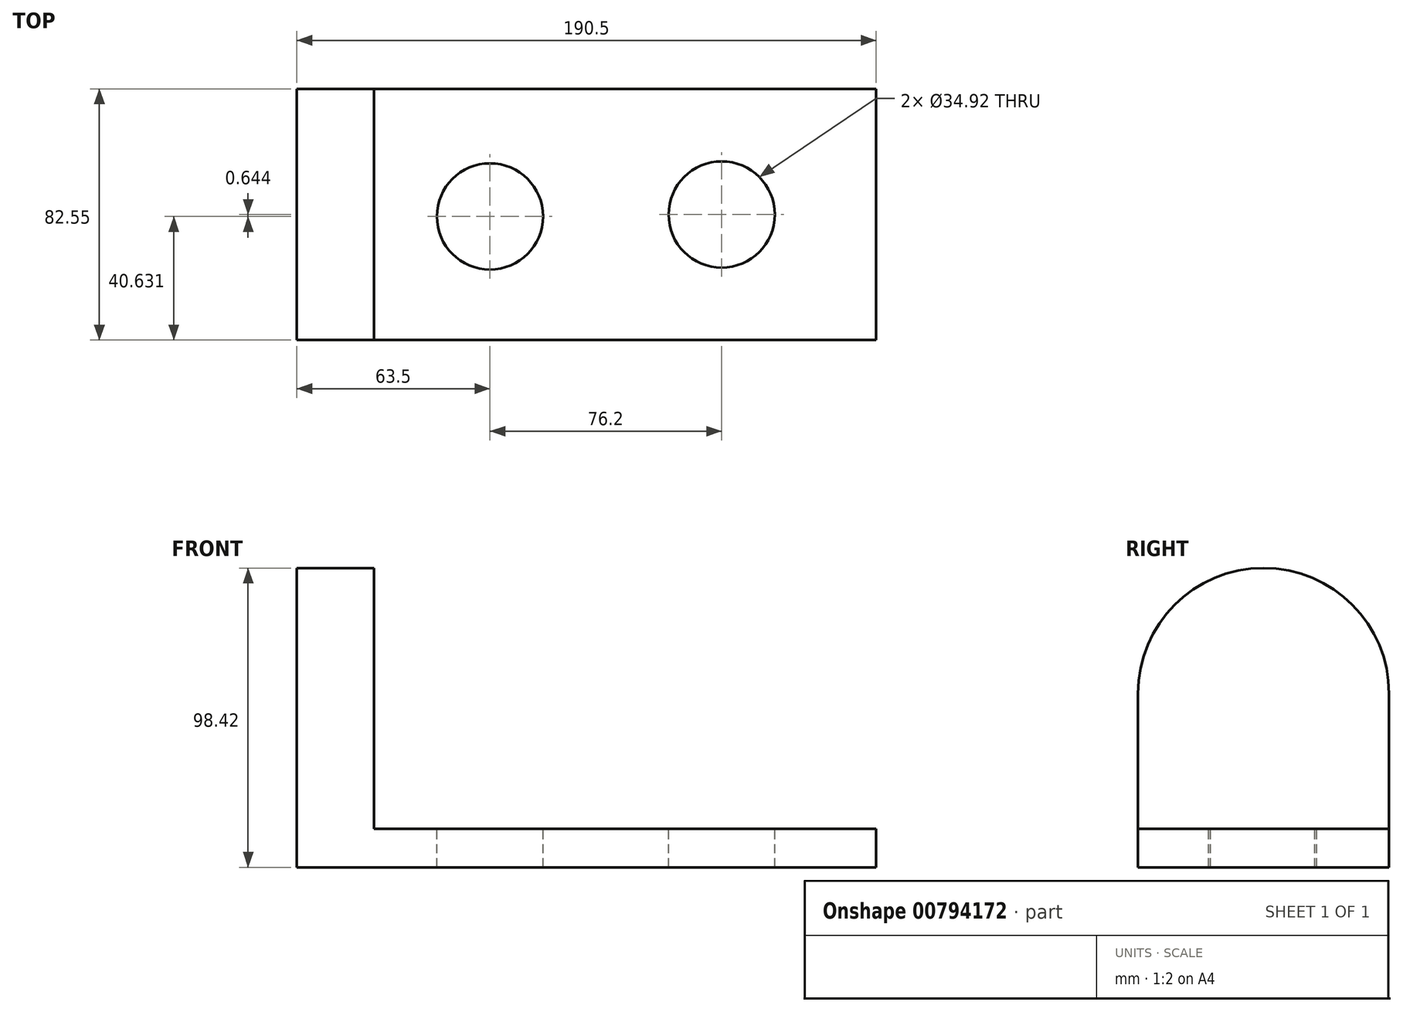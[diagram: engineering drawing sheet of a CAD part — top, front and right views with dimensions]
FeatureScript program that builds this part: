
annotation { "Feature Type Name" : "Feature", "Feature Type Description" : "" }
export const myFeature = defineFeature(function(context is Context, id is Id, definition is map)
    precondition{}
    {
        {
            var Q0;
            Q0=qCreatedBy(makeId("Front.planeOp"),FACE);
            var sketch = newSketch(context, id + "F0", { "sketchPlane" : qUnion([Q0])});
            skLineSegment(sketch, "E0", {"start": v(0, 0) * mm, "end": v(190.5, 0) * mm});
            skLineSegment(sketch, "E1", {"start": v(0, 0) * mm, "end": v(0, 127) * mm});
            skLineSegment(sketch, "E2", {"start": v(190.5, 0) * mm, "end": v(190.5, 12.7) * mm});
            skLineSegment(sketch, "E3", {"start": v(190.5, 12.7) * mm, "end": v(25.4, 12.7) * mm});
            skLineSegment(sketch, "E4", {"start": v(0, 127) * mm, "end": v(25.4, 127) * mm});
            skLineSegment(sketch, "E5", {"start": v(25.4, 127) * mm, "end": v(25.4, 12.7) * mm});
            skSolve(sketch);
        }
        {
            var Q0;
            Q0 = qSketchRegion(id + "F0", true);
            extrude(context, id + "F1", {"entities" : qUnion([Q0]), "depth" : 82.55 * mm, "offsetDistance" : 25.4 * mm});
        }
        {
            var Q0;
            Q0=makeQuery(id+"F1.opExtrude","SWEPT_FACE",FACE,{"disambiguationData":[OSD([sQuery(id+"F0.wireOp",EDGE,"E1")])]});
            var sketch = newSketch(context, id + "F2", { "sketchPlane" : qUnion([Q0])});
            skLineSegment(sketch, "E6", {"start": v(0, 0) * mm, "end": v(0, 57.15) * mm});
            skLineSegment(sketch, "E7", {"start": v(82.55, 0) * mm, "end": v(82.55, 57.15) * mm});
            skArc(sketch, "E8", {"start": v(82.55, 57.15) * mm, "mid": v(41.28, 98.43) * mm, "end": v(0, 57.15) * mm});
            skSolve(sketch);
        }
        {
            var Q0;
            {var subQ0=sQuery(id+"F2.wireOp",EDGE,"E8");Q0=makeQuery(id+"F2.imprint","IMPRINT",FACE,{"disambiguationData":[TD([[makeQuery(id+"F2.imprint","IMPRINT",EDGE,{"derivedFrom":subQ0}),-1.0]])]});}
            extrude(context, id + "F3", {"entities" : qUnion([Q0]), "operationType" : NewBodyOperationType.REMOVE, "oppositeDirection" : true, "depth" : 25.4 * mm, "offsetDistance" : 25.4 * mm});
        }
        {
            var Q0;
            Q0=makeQuery(id+"F1.opExtrude","SWEPT_FACE",FACE,{"disambiguationData":[OSD([sQuery(id+"F0.wireOp",EDGE,"E3")])]});
            var sketch = newSketch(context, id + "F4", { "sketchPlane" : qUnion([Q0])});
            skLineSegment(sketch, "E9", {"start": v(25.4, -41.28) * mm, "end": v(190.5, -41.28) * mm, "construction": true});
            skLineSegment(sketch, "E10", {"start": v(25.4, 0) * mm, "end": v(63.5, 0) * mm, "construction": true});
            skLineSegment(sketch, "E11", {"start": v(63.5, -1.29) * mm, "end": v(63.5, -82.55) * mm, "construction": true});
            skLineSegment(sketch, "E12", {"start": v(63.5, -82.55) * mm, "end": v(139.7, -82.55) * mm, "construction": true});
            skLineSegment(sketch, "E13", {"start": v(139.7, -82.55) * mm, "end": v(139.7, 0) * mm, "construction": true});
            skCircle(sketch, "E14", {"center": v(63.5, -41.92) * mm, "radius": 17.46 * mm});
            skCircle(sketch, "E15", {"center": v(139.7, -41.28) * mm, "radius": 17.46 * mm});
            skSolve(sketch);
        }
        {
            var Q0;
            Q0=makeQuery(id+"F4.imprint","IMPRINT",FACE,{"disambiguationData":[TD([[makeQuery(id+"F4.imprint","IMPRINT",EDGE,{"derivedFrom":sQuery(id+"F4.wireOp",EDGE,"E14")}),1.0]])]});
            var Q1;
            Q1=makeQuery(id+"F4.imprint","IMPRINT",FACE,{"disambiguationData":[TD([[makeQuery(id+"F4.imprint","IMPRINT",EDGE,{"derivedFrom":sQuery(id+"F4.wireOp",EDGE,"E15")}),1.0]])]});
            extrude(context, id + "F5", {"entities" : qUnion([Q0, Q1]), "operationType" : NewBodyOperationType.REMOVE, "oppositeDirection" : true, "depth" : 12.7 * mm, "offsetDistance" : 25.4 * mm});
        }
    });
